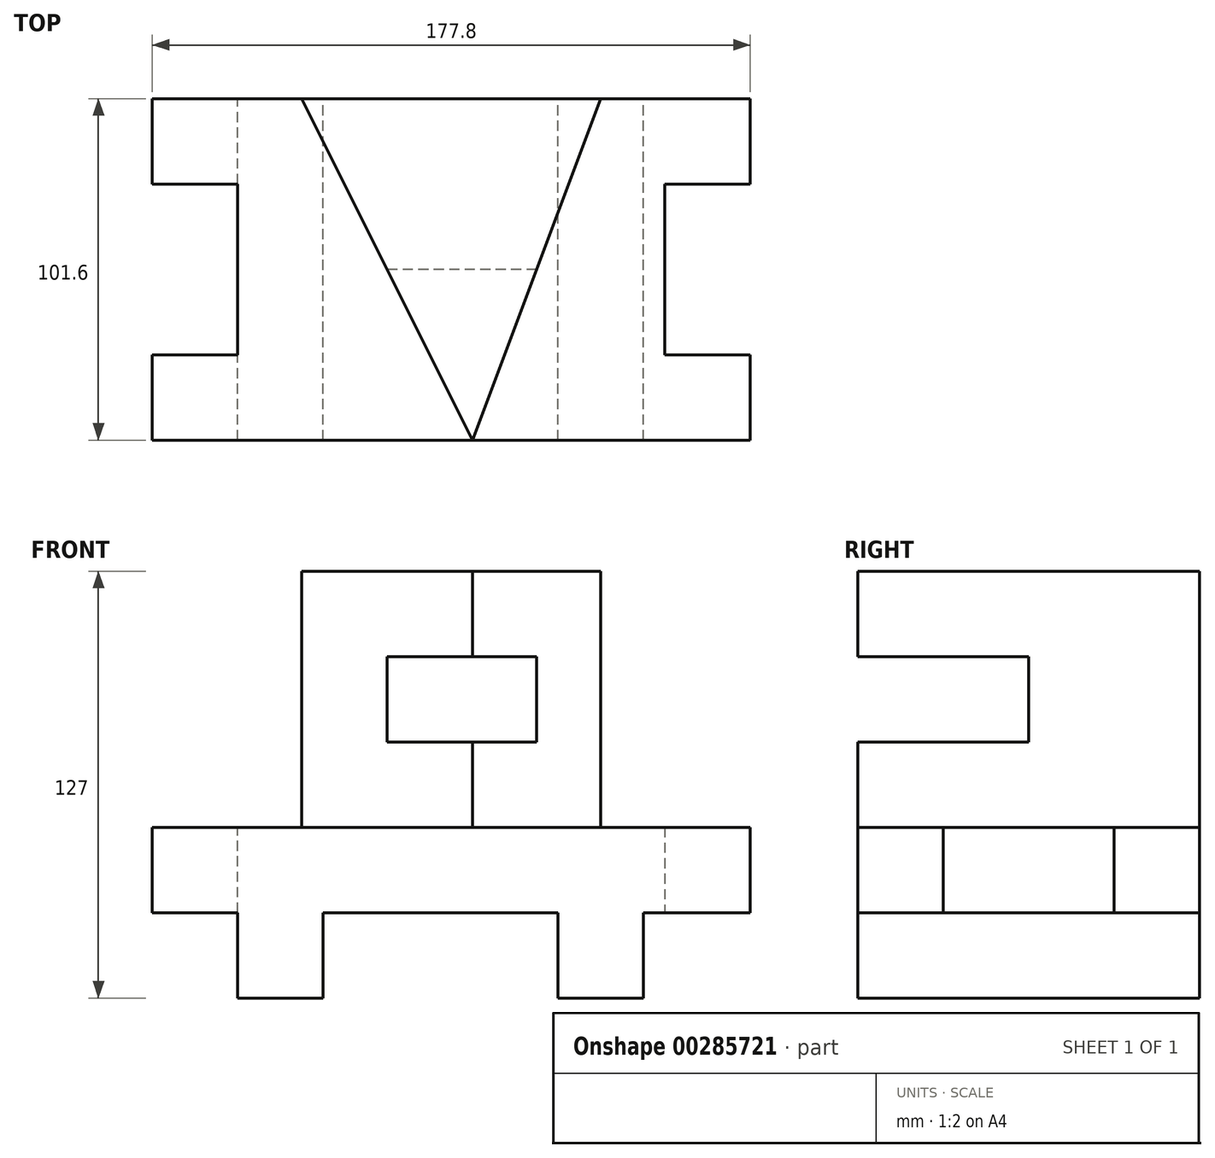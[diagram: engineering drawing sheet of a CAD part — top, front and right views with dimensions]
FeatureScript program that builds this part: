
annotation { "Feature Type Name" : "Feature", "Feature Type Description" : "" }
export const myFeature = defineFeature(function(context is Context, id is Id, definition is map)
    precondition{}
    {
        {
            var Q0;
            Q0=qCreatedBy(makeId("Front.planeOp"),FACE);
            var sketch = newSketch(context, id + "F0", { "sketchPlane" : qUnion([Q0])});
            skLineSegment(sketch, "E0", {"start": v(0, 0) * mm, "end": v(25.4, 0) * mm});
            skLineSegment(sketch, "E1", {"start": v(25.4, 0) * mm, "end": v(25.4, -25.4) * mm});
            skLineSegment(sketch, "E2", {"start": v(25.4, -25.4) * mm, "end": v(50.8, -25.4) * mm});
            skLineSegment(sketch, "E3", {"start": v(50.8, -25.4) * mm, "end": v(50.8, 0) * mm});
            skLineSegment(sketch, "E4", {"start": v(50.8, 0) * mm, "end": v(120.65, 0) * mm});
            skLineSegment(sketch, "E5", {"start": v(120.65, 0) * mm, "end": v(120.65, -25.4) * mm});
            skLineSegment(sketch, "E6", {"start": v(120.65, -25.4) * mm, "end": v(146.05, -25.4) * mm});
            skLineSegment(sketch, "E7", {"start": v(146.05, -25.4) * mm, "end": v(146.05, 0) * mm});
            skLineSegment(sketch, "E8", {"start": v(146.05, 0) * mm, "end": v(171.45, 0) * mm});
            skLineSegment(sketch, "E9", {"start": v(0, 0) * mm, "end": v(0, 25.4) * mm});
            skLineSegment(sketch, "E10", {"start": v(0, 25.4) * mm, "end": v(177.8, 25.4) * mm});
            skLineSegment(sketch, "E11", {"start": v(177.8, 25.4) * mm, "end": v(177.8, 0) * mm});
            skLineSegment(sketch, "E12", {"start": v(177.8, 0) * mm, "end": v(171.45, 0) * mm});
            skSolve(sketch);
        }
        {
            var Q0;
            Q0=makeQuery(id+"F0.imprint","IMPRINT",FACE,{"disambiguationData":[TD([[makeQuery(id+"F0.imprint","IMPRINT",EDGE,{"derivedFrom":sQuery(id+"F0.wireOp",EDGE,"E0")}),1.0]])]});
            extrude(context, id + "F1", {"entities" : qUnion([Q0]), "depth" : 101.6 * mm});
        }
        {
            var Q0;
            Q0=makeQuery(id+"F1.opExtrude","SWEPT_FACE",FACE,{"disambiguationData":[OSD([sQuery(id+"F0.wireOp",EDGE,"E11")])]});
            var sketch = newSketch(context, id + "F2", { "sketchPlane" : qUnion([Q0])});
            skLineSegment(sketch, "E13", {"start": v(-101.6, 25.4) * mm, "end": v(-76.2, 25.4) * mm});
            skLineSegment(sketch, "E14", {"start": v(-76.2, 25.4) * mm, "end": v(-76.2, 0) * mm});
            skLineSegment(sketch, "E15", {"start": v(-76.2, 0) * mm, "end": v(-101.6, 0) * mm});
            skLineSegment(sketch, "E16", {"start": v(-101.6, 0) * mm, "end": v(-101.6, 25.4) * mm});
            skLineSegment(sketch, "E17", {"start": v(0, 25.4) * mm, "end": v(0, 0) * mm});
            skLineSegment(sketch, "E18", {"start": v(0, 0) * mm, "end": v(-25.4, 0) * mm});
            skLineSegment(sketch, "E19", {"start": v(-25.4, 0) * mm, "end": v(-25.4, 25.4) * mm});
            skLineSegment(sketch, "E20", {"start": v(-25.4, 25.4) * mm, "end": v(0, 25.4) * mm});
            skSolve(sketch);
        }
        {
            var Q0;
            {var subQ0=sQuery(id+"F2.wireOp",EDGE,"E14");Q0=makeQuery(id+"F2.imprint","IMPRINT",FACE,{"disambiguationData":[TD([[makeQuery(id+"F2.imprint","IMPRINT",EDGE,{"derivedFrom":subQ0}),1.0]])]});}
            extrude(context, id + "F3", {"entities" : qUnion([Q0]), "operationType" : NewBodyOperationType.REMOVE, "oppositeDirection" : true, "depth" : 25.4 * mm});
        }
        {
            var Q0;
            Q0=makeQuery(id+"F1.opExtrude","SWEPT_FACE",FACE,{"disambiguationData":[OSD([sQuery(id+"F0.wireOp",EDGE,"E9")])]});
            var sketch = newSketch(context, id + "F4", { "sketchPlane" : qUnion([Q0])});
            skLineSegment(sketch, "E21", {"start": v(0, 25.4) * mm, "end": v(25.4, 25.4) * mm});
            skLineSegment(sketch, "E22", {"start": v(25.4, 25.4) * mm, "end": v(25.4, 0) * mm});
            skLineSegment(sketch, "E23", {"start": v(25.4, 0) * mm, "end": v(0, 0) * mm});
            skLineSegment(sketch, "E24", {"start": v(0, 0) * mm, "end": v(0, 25.4) * mm});
            skLineSegment(sketch, "E25", {"start": v(101.6, 25.4) * mm, "end": v(101.6, 0) * mm});
            skLineSegment(sketch, "E26", {"start": v(101.6, 0) * mm, "end": v(76.2, 0) * mm});
            skLineSegment(sketch, "E27", {"start": v(76.2, 0) * mm, "end": v(76.2, 25.4) * mm});
            skLineSegment(sketch, "E28", {"start": v(76.2, 25.4) * mm, "end": v(101.6, 25.4) * mm});
            skSolve(sketch);
        }
        {
            var Q0;
            {var subQ0=sQuery(id+"F4.wireOp",EDGE,"E22");Q0=makeQuery(id+"F4.imprint","IMPRINT",FACE,{"disambiguationData":[TD([[makeQuery(id+"F4.imprint","IMPRINT",EDGE,{"derivedFrom":subQ0}),1.0]])]});}
            extrude(context, id + "F5", {"entities" : qUnion([Q0]), "operationType" : NewBodyOperationType.REMOVE, "oppositeDirection" : true, "depth" : 25.4 * mm});
        }
        {
            var Q0;
            Q0=makeQuery(id+"F1.opExtrude","SWEPT_FACE",FACE,{"disambiguationData":[OSD([sQuery(id+"F0.wireOp",EDGE,"E10")])]});
            var sketch = newSketch(context, id + "F6", { "sketchPlane" : qUnion([Q0])});
            skLineSegment(sketch, "E29", {"start": v(0, -101.6) * mm, "end": v(95.25, -101.6) * mm});
            skLineSegment(sketch, "E30", {"start": v(177.8, 0) * mm, "end": v(133.35, 0) * mm});
            skLineSegment(sketch, "E31", {"start": v(133.35, 0) * mm, "end": v(95.25, -101.6) * mm});
            skLineSegment(sketch, "E32", {"start": v(0, 0) * mm, "end": v(44.45, 0) * mm});
            skLineSegment(sketch, "E33", {"start": v(44.45, 0) * mm, "end": v(95.25, -101.6) * mm});
            skSolve(sketch);
        }
        {
            var Q0;
            {var subQ0=sQuery(id+"F6.wireOp",EDGE,"E31");Q0=makeQuery(id+"F6.imprint","IMPRINT",FACE,{"disambiguationData":[TD([[makeQuery(id+"F6.imprint","IMPRINT",EDGE,{"derivedFrom":subQ0}),-1.0]])]});}
            extrude(context, id + "F7", {"entities" : qUnion([Q0]), "operationType" : NewBodyOperationType.ADD, "depth" : 76.2 * mm});
        }
        {
            var Q0;
            Q0=qCreatedBy(makeId("Right.planeOp"),FACE);
            var sketch = newSketch(context, id + "F8", { "sketchPlane" : qUnion([Q0])});
            skLineSegment(sketch, "E34", {"start": v(-101.6, 25.4) * mm, "end": v(-50.8, 25.4) * mm});
            skLineSegment(sketch, "E35", {"start": v(-50.8, 25.4) * mm, "end": v(-50.8, 101.6) * mm});
            skPoint(sketch, "E35.endSnap0", {"position": v(-50.8, 101.6) * mm});
            skLineSegment(sketch, "E36", {"start": v(-50.8, 101.6) * mm, "end": v(-101.6, 101.6) * mm});
            skLineSegment(sketch, "E37", {"start": v(-50.8, 25.4) * mm, "end": v(-50.8, 50.8) * mm});
            skLineSegment(sketch, "E38", {"start": v(-50.8, 50.8) * mm, "end": v(-101.6, 50.8) * mm});
            skLineSegment(sketch, "E39", {"start": v(-50.8, 50.8) * mm, "end": v(-50.8, 76.2) * mm});
            skLineSegment(sketch, "E40", {"start": v(-50.8, 76.2) * mm, "end": v(-101.6, 76.2) * mm});
            skLineSegment(sketch, "E41", {"start": v(-101.6, 76.2) * mm, "end": v(-101.6, 50.8) * mm});
            skSolve(sketch);
        }
        {
            var Q0;
            Q0=makeQuery(id+"F8.imprint","IMPRINT",FACE,{"disambiguationData":[TD([[makeQuery(id+"F8.imprint","IMPRINT",EDGE,{"derivedFrom":sQuery(id+"F8.wireOp",EDGE,"E38")}),-1.0]])]});
            extrude(context, id + "F9", {"entities" : qUnion([Q0]), "operationType" : NewBodyOperationType.REMOVE, "depth" : 254 * mm});
        }
    });
